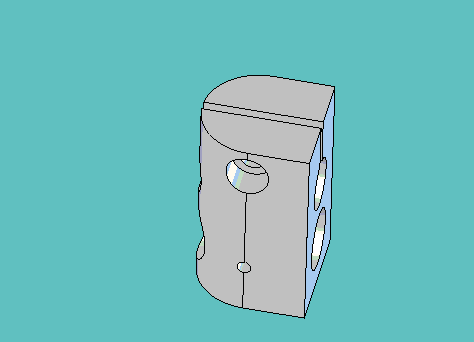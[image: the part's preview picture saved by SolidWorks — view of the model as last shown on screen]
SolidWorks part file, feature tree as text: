
SOLIDWORKS PART (.sldprt)
format: sldprt  version: not decoded by parser v0  size: 637,440 bytes
history: native  units: mm
features: sketch x11, extrude x9, revolve x2, material x1, plane x1, boolean_combine x1 (+11 scaffold rows collapsed)
feature tree (36):
  scaffold x11  (default folders/planes/origin — collapsed)
  material  "Material <not specified>"
  sketch  "Sketch1"  dims[D1=33.3375mm D2=9.525mm D3=153.9875mm]
  revolve  "Revolve1"  Angle=360deg
  sketch  "Sketch14"  dims[D1=10.16mm]
  extrude  "Extrude8"  [1 undecoded]
  sketch  "Sketch2"  dims[c1.D1=3.4544mm c1.D2=2.2606mm c1.D3=8.7376mm c1.D4=28.3464mm c2.D3=8.7376mm c2.D4=28.3464mm]
  extrude  "Extrude1"  [1 undecoded]
  sketch  "Sketch3"  dims[D1=2.2606mm]
  extrude  "Extrude2"  Depth=7.9756mm
  sketch  "Sketch5"  dims[c1.D4=~4.437453mm c1.D5=6.35mm c1.D1=8.7376mm c1.D2=6.35mm c1.D3=6.35mm c2.D4=9.525mm c2.D2=6.35mm c3.D4=9.525mm c3.D6=12.7mm c4.D4=9.525mm c4.D1=8.7376mm c4.D3=6.35mm c5.D4=6.35mm c5.D1=8.7376mm c5.D3=6.35mm c6.D1=8.7376mm c6.D3=6.35mm c7.D1=9.525mm c7.D4=8.7376mm c8.D1=8.7376mm c8.D2=6.35mm c8.D4=12.7mm]
  revolve  "Revolve2"  Angle=360deg
  sketch  "Sketch11"  dims[D1=11.1125mm]
  sketch  "Sketch6"  dims[D1=~8.73125mm D2=20.6502mm]
  extrude  "Extrude3"  [1 undecoded]
  sketch  "Sketch9"  dims[c1.D1=4.3688mm c1.D2=2.2606mm c1.D3=8.7376mm c1.D4=28.3464mm c2.D3=8.7376mm c2.D4=28.3464mm]
  extrude  "Extrude5"  [1 undecoded]
  plane  "Plane1"  Offset=12.7mm
  sketch  "Sketch10"  dims[D1=~7.14375mm]
  extrude  "Extrude6"  Depth=7.9375mm
  sketch  "Sketch13"  dims[D1=~0.79375mm D2=~0.79375mm]
  extrude  "Extrude7"  Depth=12.7mm
  extrude  "Extrude9"  [1 undecoded]
  sketch  "Sketch15"  dims[D1=2.159mm D2=2.159mm]
  extrude  "Extrude10"  Depth=4.7625mm
  boolean_combine  "Combine1"
decode coverage: 17 of 23 modeling features carry decoded parameters
note: ~ marks probable driven/reference dimensions
note: 5 parameter values undecoded
summary: no parameter record found for 5 features
note: suppression state not decoded; provenance and decode notes live in map.json
